# Revit family: Shower_System-Symmons-Dia-Hand_Shower-Trim
name_source: partatom
category: Plumbing Fixtures
revit_build: Autodesk Revit 2015 (Build: 20140606_1530(x64)
units: mm (PartAtom-declared; Revit-internal decimal feet)

## types (2) — shared parameters
Date Modified = January 30, 2015
Default Elevation = 32 "
Family Version = 1.0
Gallons Per Minute = 2.500 GPM
Manufacturer = Symmons Industries, Inc.
Model Disclaimer = Contact Symmons Industries, Inc. For More Information
Product Documentation Link = http://www.symmons.com
Product Page URL = http://www.symmons.com
Product data url = https://bimobject.com
URL = http://www.symmons.com
z GPM GPM = 1.000 GPM
z GPM Number = 2.5
z Has Trim = Yes
z Type GPM = 2.5

## per-type parameters (varying)
| type | Description | Equipment Abbreviation | Model | Product Material | z Type | z Type Finish | z Valve |
| 2.5 GPM Flow Restrictor, Chrome | Trim only, mixing valve ordered separately, Chrome | TSS | 3503-H321-V-CYL-B-TRM | Chrome - Symmons - Polished | 1 | 1 | Shower_System_Valve-Symmons-Dia-Shower-Trim : Trim, Chrome |
| 2.5 GPM Flow Restrictor, Satin Nickel | Trim only, mixing valve ordered separately, Satin Nickel | SSV | 3503-H321-V-CYL-B-STN-TRM | Nickel - Symmons - Satin | 2 | 2 | Shower_System_Valve-Symmons-Dia-Shower-Trim : Trim, Satin Nickel |

## geometry (parser evidence)
native form markers: Blend x2, Sweep x8
no freeform markers — native parametric forms only
